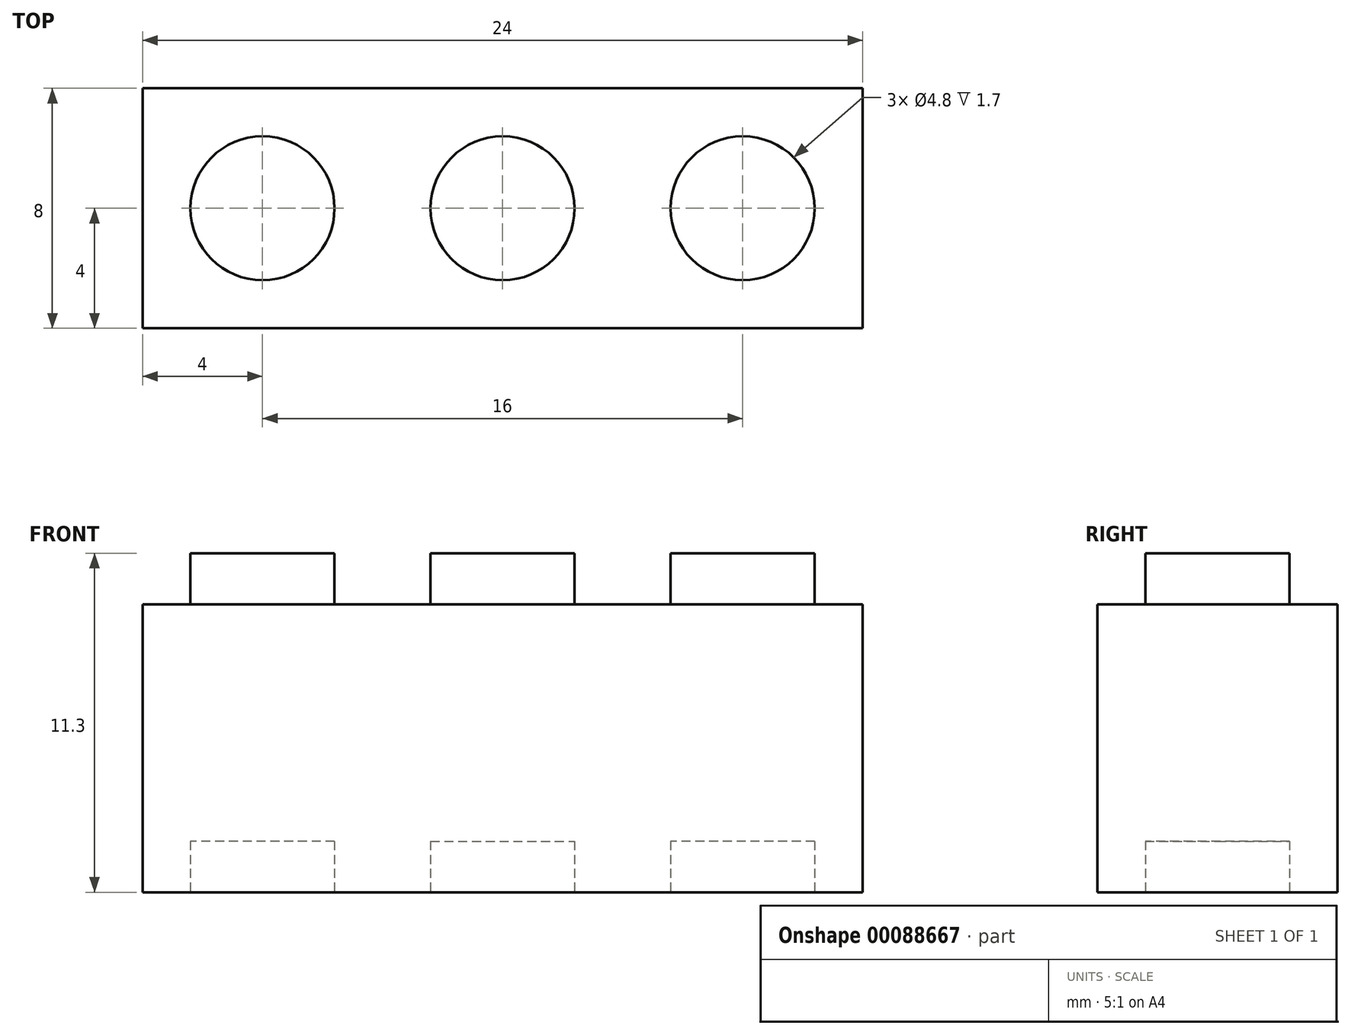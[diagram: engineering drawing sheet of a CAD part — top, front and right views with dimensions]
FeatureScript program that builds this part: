
annotation { "Feature Type Name" : "Feature", "Feature Type Description" : "" }
export const myFeature = defineFeature(function(context is Context, id is Id, definition is map)
    precondition{}
    {
        {
            var Q0;
            Q0=qCreatedBy(makeId("Front.planeOp"),FACE);
            var sketch = newSketch(context, id + "F0", { "sketchPlane" : qUnion([Q0])});
            skLineSegment(sketch, "E0.bottom", {"start": v(-4, 9.6) * mm, "end": v(-2.4, 9.6) * mm});
            skLineSegment(sketch, "E0.top", {"start": v(-4, 0) * mm, "end": v(4, 0) * mm});
            skLineSegment(sketch, "E0.left", {"start": v(-4, 9.6) * mm, "end": v(-4, 0) * mm});
            skLineSegment(sketch, "E0.right", {"start": v(4, 9.6) * mm, "end": v(4, 0) * mm});
            skLineSegment(sketch, "E1.top", {"start": v(-2.4, 11.3) * mm, "end": v(2.4, 11.3) * mm});
            skLineSegment(sketch, "E1.left", {"start": v(-2.4, 9.6) * mm, "end": v(-2.4, 11.3) * mm});
            skLineSegment(sketch, "E1.right", {"start": v(2.4, 9.6) * mm, "end": v(2.4, 11.3) * mm});
            skLineSegment(sketch, "E2", {"start": v(0, 0) * mm, "end": v(0, 24.04) * mm, "construction": true});
            skLineSegment(sketch, "E3.trimOffspring", {"start": v(2.4, 9.6) * mm, "end": v(4, 9.6) * mm});
            skSolve(sketch);
        }
        {
            var Q0;
            Q0=makeQuery(id+"F0.imprint","IMPRINT",FACE,{"disambiguationData":[TD([[makeQuery(id+"F0.imprint","IMPRINT",EDGE,{"derivedFrom":sQuery(id+"F0.wireOp",EDGE,"E0.bottom")}),-1.0]])]});
            extrude(context, id + "F1", {"entities" : qUnion([Q0]), "depth" : 8 * mm});
        }
        {
            var Q0;
            Q0=qCreatedBy(makeId("Top.planeOp"),FACE);
            var Q1;
            Q1=makeQuery(id+"F1.opExtrude","CAP_VERTEX",VERTEX,{"disambiguationData":[OSD([sQuery(id+"F0.wireOp",EDGE,"E1.top"),sQuery(id+"F0.wireOp",EDGE,"E1.right")])],"isStart":true});
            cPlane(context, id + "F2", {"entities" : qUnion([Q0, Q1]), "cplaneType" : CPlaneType.PLANE_POINT, "offset" : 152.4 * mm, "width" : 152.4 * mm, "height" : 152.4 * mm});
        }
        {
            var Q0;
            Q0=qCreatedBy(id+"F2.planeOp",FACE);
            var sketch = newSketch(context, id + "F3", { "sketchPlane" : qUnion([Q0])});
            skLineSegment(sketch, "E4.0", {"start": v(-4, -8) * mm, "end": v(-4, 0) * mm});
            skLineSegment(sketch, "E5.0", {"start": v(4, -8) * mm, "end": v(4, 0) * mm});
            skLineSegment(sketch, "E6", {"start": v(-4, 0) * mm, "end": v(4, 0) * mm});
            skLineSegment(sketch, "E7", {"start": v(-4, -8) * mm, "end": v(4, -8) * mm});
            skLineSegment(sketch, "E8", {"start": v(-4, 0) * mm, "end": v(4, -8) * mm, "construction": true});
            skLineSegment(sketch, "E9", {"start": v(-4, -8) * mm, "end": v(4, 0) * mm, "construction": true});
            skCircle(sketch, "E10", {"center": v(0, -4) * mm, "radius": 2.4 * mm});
            skSolve(sketch);
        }
        {
            var Q0;
            Q0=qSketchRegion(id+"F3",true);
            var Q1;
            Q1=makeQuery(id+"F1.opExtrude","SWEPT_FACE",FACE,{"disambiguationData":[OSD([sQuery(id+"F0.wireOp",EDGE,"E0.bottom")])]});
            extrude(context, id + "F4", {"entities" : qUnion([Q0]), "operationType" : NewBodyOperationType.REMOVE, "endBound" : BoundingType.UP_TO_SURFACE, "oppositeDirection" : true, "endBoundEntityFace" : qUnion([Q1]), "depth" : 25.4 * mm});
        }
        {
            var Q0;
            Q0=qCreatedBy(makeId("Top.planeOp"),FACE);
            var sketch = newSketch(context, id + "F5", { "sketchPlane" : qUnion([Q0])});
            skCircle(sketch, "E11.0", {"center": v(0, -4) * mm, "radius": 2.4 * mm});
            skSolve(sketch);
        }
        {
            var Q0;
            Q0=makeQuery(id+"F5.imprint","IMPRINT",FACE,{"disambiguationData":[TD([[makeQuery(id+"F5.imprint","IMPRINT",EDGE,{"derivedFrom":sQuery(id+"F5.wireOp",EDGE,"E11.0")}),1.0]])]});
            extrude(context, id + "F6", {"entities" : qUnion([Q0]), "operationType" : NewBodyOperationType.REMOVE, "depth" : 1.7 * mm});
        }
        {
            var Q0;
            Q0=qCreatedBy(makeId("Right.planeOp"),FACE);
            var Q1;
            Q1=makeQuery(id+"F1.opExtrude","CAP_VERTEX",VERTEX,{"disambiguationData":[OSD([sQuery(id+"F0.wireOp",EDGE,"E0.right"),sQuery(id+"F0.wireOp",EDGE,"E3.trimOffspring")])],"isStart":false});
            cPlane(context, id + "F7", {"entities" : qUnion([Q0, Q1]), "cplaneType" : CPlaneType.PLANE_POINT, "offset" : 152.4 * mm, "width" : 152.4 * mm, "height" : 152.4 * mm});
        }
        {
            var Q0;
            Q0=makeQuery(id+"F1.opExtrude","SWEPT_BODY",BODY,{"disambiguationData":[OSD([sQuery(id+"F0.wireOp",EDGE,"E0.bottom"),sQuery(id+"F0.wireOp",EDGE,"E0.top"),sQuery(id+"F0.wireOp",EDGE,"E0.left"),sQuery(id+"F0.wireOp",EDGE,"E0.right"),sQuery(id+"F0.wireOp",EDGE,"E1.top"),sQuery(id+"F0.wireOp",EDGE,"E1.left"),sQuery(id+"F0.wireOp",EDGE,"E1.right"),sQuery(id+"F0.wireOp",EDGE,"E3.trimOffspring")])]});
            var Q1;
            Q1=qCreatedBy(id+"F7.planeOp",FACE);
            mirror(context, id + "F8", {"operationType" : NewBodyOperationType.ADD, "entities" : qUnion([Q0]), "mirrorPlane" : qUnion([Q1])});
        }
        {
            var Q0;
            Q0=qCreatedBy(id+"F7.planeOp",FACE);
            var Q1;
            Q1=makeQuery(id+"F8.opPattern","COPY",VERTEX,{"derivedFrom":makeQuery(id+"F1.opExtrude","CAP_VERTEX",VERTEX,{"disambiguationData":[OSD([sQuery(id+"F0.wireOp",EDGE,"E0.bottom"),sQuery(id+"F0.wireOp",EDGE,"E0.left")])],"isStart":false}),"instanceName":"1"});
            cPlane(context, id + "F9", {"entities" : qUnion([Q0, Q1]), "cplaneType" : CPlaneType.PLANE_POINT, "offset" : 152.4 * mm, "width" : 152.4 * mm, "height" : 152.4 * mm});
        }
        {
            var Q0;
            Q0=makeQuery(id+"F1.opExtrude","SWEPT_BODY",BODY,{"disambiguationData":[OSD([sQuery(id+"F0.wireOp",EDGE,"E0.bottom"),sQuery(id+"F0.wireOp",EDGE,"E0.top"),sQuery(id+"F0.wireOp",EDGE,"E0.left"),sQuery(id+"F0.wireOp",EDGE,"E0.right"),sQuery(id+"F0.wireOp",EDGE,"E1.top"),sQuery(id+"F0.wireOp",EDGE,"E1.left"),sQuery(id+"F0.wireOp",EDGE,"E1.right"),sQuery(id+"F0.wireOp",EDGE,"E3.trimOffspring")])]});
            var Q1;
            Q1=qCreatedBy(id+"F9.planeOp",FACE);
            mirror(context, id + "F10", {"operationType" : NewBodyOperationType.ADD, "entities" : qUnion([Q0]), "mirrorPlane" : qUnion([Q1])});
        }
        {
            var Q0;
            Q0=makeQuery(id+"F10.opPattern","COPY",FACE,{"derivedFrom":makeQuery(id+"F1.opExtrude","SWEPT_FACE",FACE,{"disambiguationData":[OSD([sQuery(id+"F0.wireOp",EDGE,"E0.left")])]}),"instanceName":"1"});
            var sketch = newSketch(context, id + "F11", { "sketchPlane" : qUnion([Q0])});
            skLineSegment(sketch, "E12.bottom", {"start": v(4.8, 15.71) * mm, "end": v(-13.54, 15.71) * mm});
            skLineSegment(sketch, "E12.top", {"start": v(4.8, -2.89) * mm, "end": v(-13.54, -2.89) * mm});
            skLineSegment(sketch, "E12.left", {"start": v(4.8, 15.71) * mm, "end": v(4.8, -2.89) * mm});
            skLineSegment(sketch, "E12.right", {"start": v(-13.54, 15.71) * mm, "end": v(-13.54, -2.89) * mm});
            skPoint(sketch, "E12.middle", {"position": v(-4.37, 6.41) * mm});
            skSolve(sketch);
        }
        {
            var Q0;
            Q0 = qSketchRegion(id + "F11", true);
            extrude(context, id + "F12", {"entities" : qUnion([Q0]), "operationType" : NewBodyOperationType.REMOVE, "oppositeDirection" : true, "depth" : 8 * mm, "offsetDistance" : 25.4 * mm});
        }
    });
